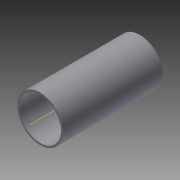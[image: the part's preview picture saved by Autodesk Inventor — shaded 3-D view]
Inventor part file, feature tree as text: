
AUTODESK INVENTOR PART (.ipt)
format: ipt  version: 2013 (Build 170138000, 138)  size: 81,408 bytes
history: native  units: mm
features: other x2, extrude x2, sketch x2
ambient origin geometry x8: Origin, YZ Plane, XZ Plane, XY Plane, X Axis, Y Axis, Z Axis, Center Point
feature tree (6):
  other  "ソリッド1"
  extrude  "押し出し1"  Depth=70.0mm
  extrude  "押し出し2"  Depth=64.0mm
  other  "作業軸1"
  sketch  "スケッチ1"
  sketch  "スケッチ2"
